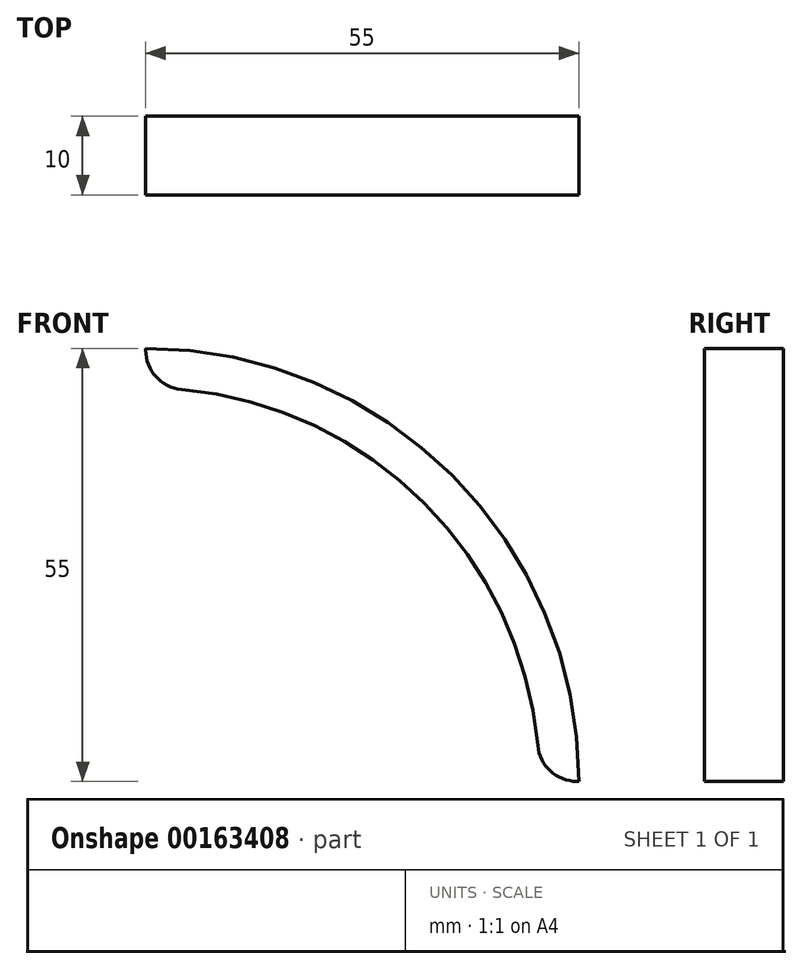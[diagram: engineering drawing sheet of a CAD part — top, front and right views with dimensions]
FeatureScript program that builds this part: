
annotation { "Feature Type Name" : "Feature", "Feature Type Description" : "" }
export const myFeature = defineFeature(function(context is Context, id is Id, definition is map)
    precondition{}
    {
        {
            var Q0;
            Q0=qCreatedBy(makeId("Front.planeOp"),FACE);
            var sketch = newSketch(context, id + "F0", { "sketchPlane" : qUnion([Q0])});
            skArc(sketch, "E0", {"start": v(50, 0) * mm, "mid": v(35.36, 35.36) * mm, "end": v(0, 50) * mm});
            skArc(sketch, "E1", {"start": v(55, 0) * mm, "mid": v(38.9, 38.9) * mm, "end": v(0, 55) * mm});
            skLineSegment(sketch, "E2", {"start": v(0, 55) * mm, "end": v(0, 50) * mm});
            skLineSegment(sketch, "E3", {"start": v(50, 0) * mm, "end": v(55, 0) * mm});
            skSolve(sketch);
        }
        {
            var Q0;
            Q0=makeQuery(id+"F0.imprint","IMPRINT",FACE,{"disambiguationData":[TD([[makeQuery(id+"F0.imprint","IMPRINT",EDGE,{"derivedFrom":sQuery(id+"F0.wireOp",EDGE,"E0")}),-1.0]])]});
            extrude(context, id + "F1", {"entities" : qUnion([Q0]), "depth" : 10 * mm});
        }
        {
            var Q0;
            Q0=makeQuery(id+"F1.opExtrude","SWEPT_EDGE",EDGE,{"disambiguationData":[OSD([sQuery(id+"F0.wireOp",EDGE,"E0"),sQuery(id+"F0.wireOp",EDGE,"E3")])]});
            var Q1;
            Q1=makeQuery(id+"F1.opExtrude","SWEPT_EDGE",EDGE,{"disambiguationData":[OSD([sQuery(id+"F0.wireOp",EDGE,"E0"),sQuery(id+"F0.wireOp",EDGE,"E2")])]});
            fillet(context, id + "F2", {"entities" : qUnion([Q0, Q1]), "radius" : 5 * mm, "tangentPropagation" : true, "allowEdgeOverflow" : false});
        }
    });
